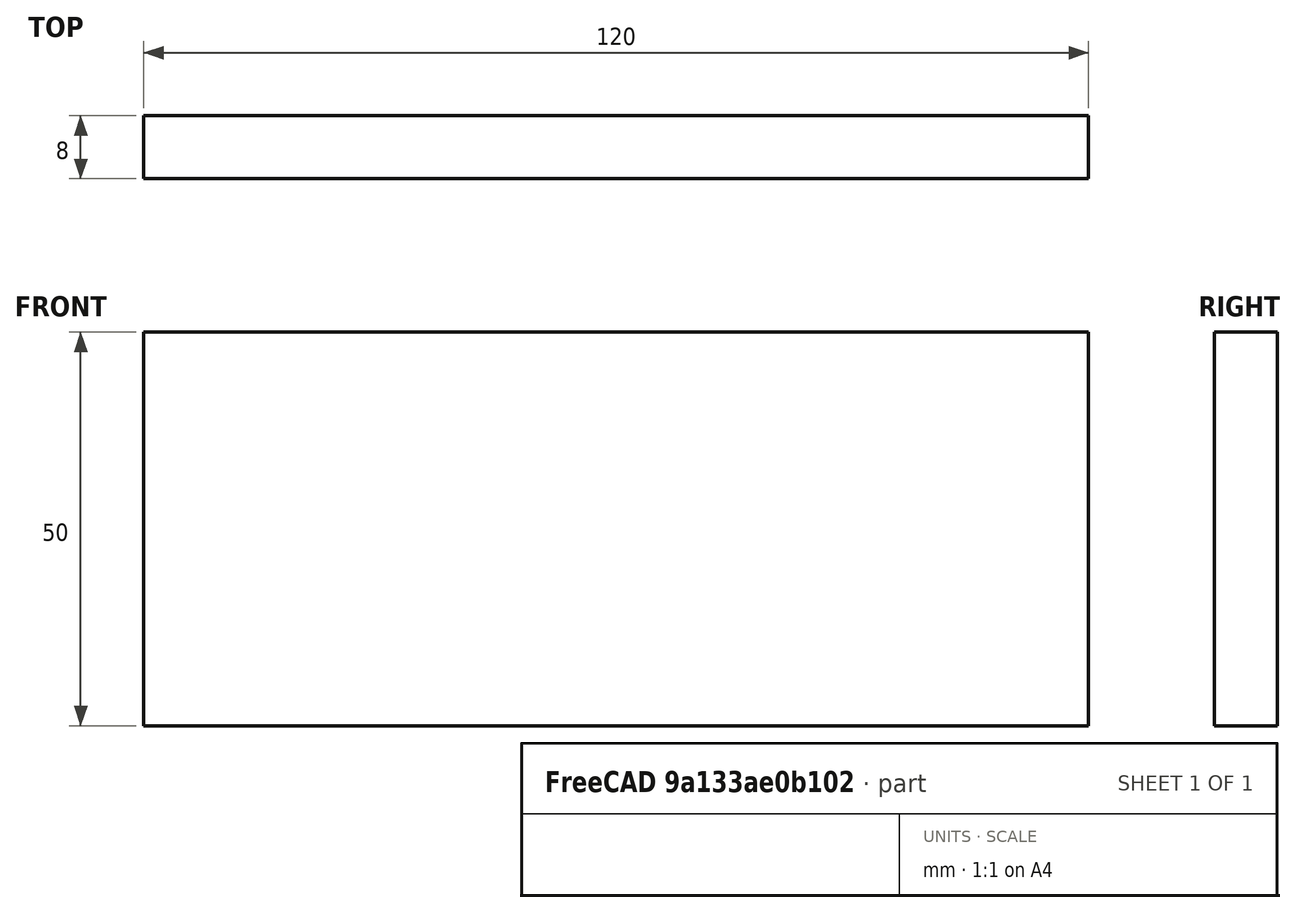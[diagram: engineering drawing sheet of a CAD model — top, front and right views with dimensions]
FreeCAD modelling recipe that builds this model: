
FCSTD DOCUMENT  (FreeCAD 0.15R4671 (Git))
Label: Flat Bar 120x8 EN10058 S235JR
License: All rights reserved
LicenseURL: http://en.wikipedia.org/wiki/All_rights_reserved
objects: Sketcher::SketchObject×1, Part::Extrusion×1
note: 2 computed .brp shape members not serialized (recipe doc carries the construction recipe); baked Part::Feature solids carry a one-line shape summary decoded from their .brp

FEATURE [Sketcher::SketchObject] Sketch
  sketch-geometry (4):
    g0: LineSegment StartX=-60 StartY=-4 StartZ=0 EndX=60 EndY=-4 EndZ=0
    g1: LineSegment StartX=60 StartY=-4 StartZ=0 EndX=60 EndY=4 EndZ=0
    g2: LineSegment StartX=60 StartY=4 StartZ=0 EndX=-60 EndY=4 EndZ=0
    g3: LineSegment StartX=-60 StartY=4 StartZ=0 EndX=-60 EndY=-4 EndZ=0
  constraints (12):
    c: Coincident(g0,g1)
    c: Coincident(g1,g2)
    c: Coincident(g2,g3)
    c: Coincident(g3,g0)
    c: Horizontal(g0)
    c: Horizontal(g2)
    c: Vertical(g1)
    c: Vertical(g3)
    c: Symmetric(g1,g2,g-2)
    c: Symmetric(g0,g1,g-1)
    c: DistanceY(g1) = 8
    c: DistanceX(g0) = 120
FEATURE [Part::Extrusion] Extrude  label="Flat Bar 120x8 EN10058 S235JR"
  Base = -> Sketch
  Dir = (0,0,50)
  Solid = true
